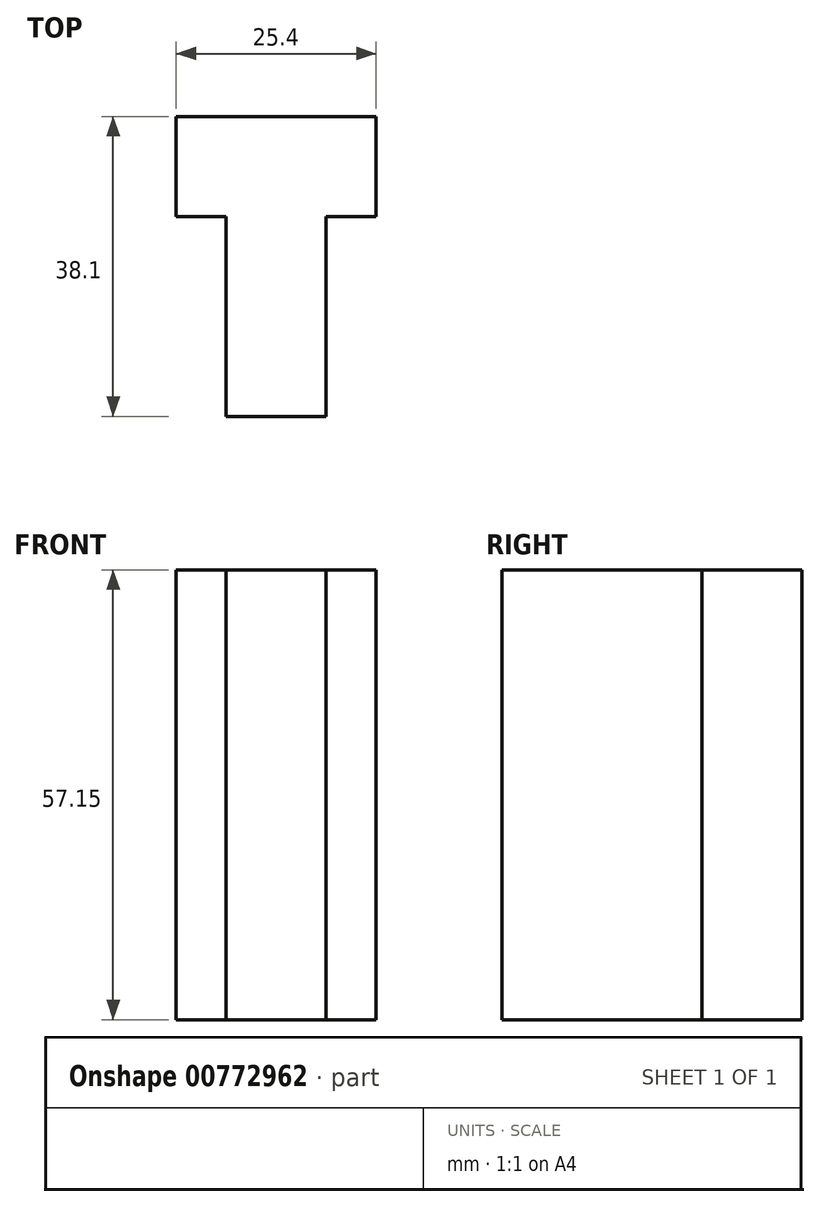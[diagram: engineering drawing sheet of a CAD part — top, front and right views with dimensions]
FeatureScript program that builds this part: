
annotation { "Feature Type Name" : "Feature", "Feature Type Description" : "" }
export const myFeature = defineFeature(function(context is Context, id is Id, definition is map)
    precondition{}
    {
        {
            var Q0;
            Q0=qCreatedBy(makeId("Top.planeOp"),FACE);
            var sketch = newSketch(context, id + "F0", { "sketchPlane" : qUnion([Q0])});
            skLineSegment(sketch, "E0", {"start": v(0, 0) * mm, "end": v(0, 25.4) * mm});
            skLineSegment(sketch, "E1", {"start": v(0, 0) * mm, "end": v(12.7, 0) * mm});
            skLineSegment(sketch, "E2", {"start": v(12.7, 0) * mm, "end": v(12.7, 25.4) * mm});
            skLineSegment(sketch, "E3", {"start": v(0, 25.4) * mm, "end": v(-6.35, 25.4) * mm});
            skLineSegment(sketch, "E4", {"start": v(12.7, 25.4) * mm, "end": v(19.05, 25.4) * mm});
            skLineSegment(sketch, "E5", {"start": v(19.05, 25.4) * mm, "end": v(19.05, 38.1) * mm});
            skLineSegment(sketch, "E6", {"start": v(-6.35, 25.4) * mm, "end": v(-6.35, 38.1) * mm});
            skLineSegment(sketch, "E7", {"start": v(-6.35, 38.1) * mm, "end": v(19.05, 38.1) * mm});
            skSolve(sketch);
        }
        {
            var Q0;
            Q0=makeQuery(id+"F0.imprint","IMPRINT",FACE,{"disambiguationData":[TD([[makeQuery(id+"F0.imprint","IMPRINT",EDGE,{"derivedFrom":sQuery(id+"F0.wireOp",EDGE,"E0")}),-1.0]])]});
            extrude(context, id + "F1", {"entities" : qUnion([Q0]), "depth" : 25.4 * mm, "offsetDistance" : 25.4 * mm});
        }
        {
            var Q0;
            Q0=makeQuery(id+"F1.opExtrude","CAP_FACE",FACE,{"disambiguationData":[OSD([sQuery(id+"F0.wireOp",EDGE,"E0"),sQuery(id+"F0.wireOp",EDGE,"E1"),sQuery(id+"F0.wireOp",EDGE,"E2"),sQuery(id+"F0.wireOp",EDGE,"E3"),sQuery(id+"F0.wireOp",EDGE,"E4"),sQuery(id+"F0.wireOp",EDGE,"E5"),sQuery(id+"F0.wireOp",EDGE,"E6"),sQuery(id+"F0.wireOp",EDGE,"E7")])],"isStart":false});
            extrude(context, id + "F2", {"entities" : qUnion([Q0]), "operationType" : NewBodyOperationType.ADD, "depth" : 31.75 * mm, "offsetDistance" : 25.4 * mm});
        }
    });
